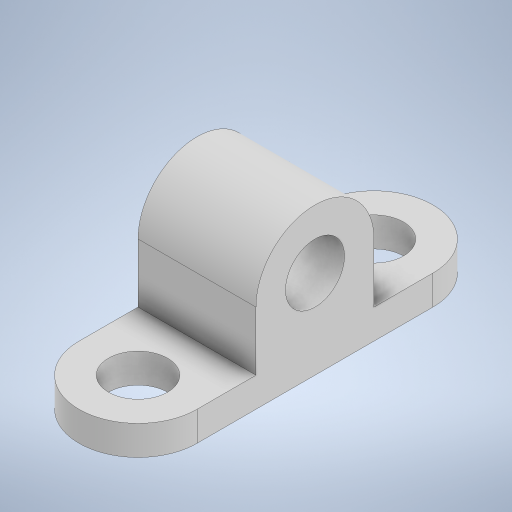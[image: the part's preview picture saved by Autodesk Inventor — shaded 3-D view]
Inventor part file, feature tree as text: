
AUTODESK INVENTOR PART (.ipt)
format: ipt  version: 2024 (Build 280153000, 153)  size: 255,488 bytes
history: native  units: in
note: dims shown in document units (in); Inventor stores cm internally (conversion verified against a paired STEP export)
features: extrude x2, sketch x2
ambient origin geometry x8: Origin, YZ Plane, XZ Plane, XY Plane, X Axis, Y Axis, Z Axis, Center Point
bodies: Solid1 (feature_tree)
feature tree (4):
  extrude  "Extrusion1"  Depth=1.5748in
  extrude  "Extrusion2"  Depth=0.7874in
  sketch  "Sketch1"  dims[d0=1.5748in d1=1.5748in]
  sketch  "Sketch2"  dims[d3=0.7874in d5=0.7874in d6=1.5748in d7=1.5748in d8=0.3937in d9=0.0in d11=1.5748in d12=0.7874in d13=1.5748in d14=0.0in]
